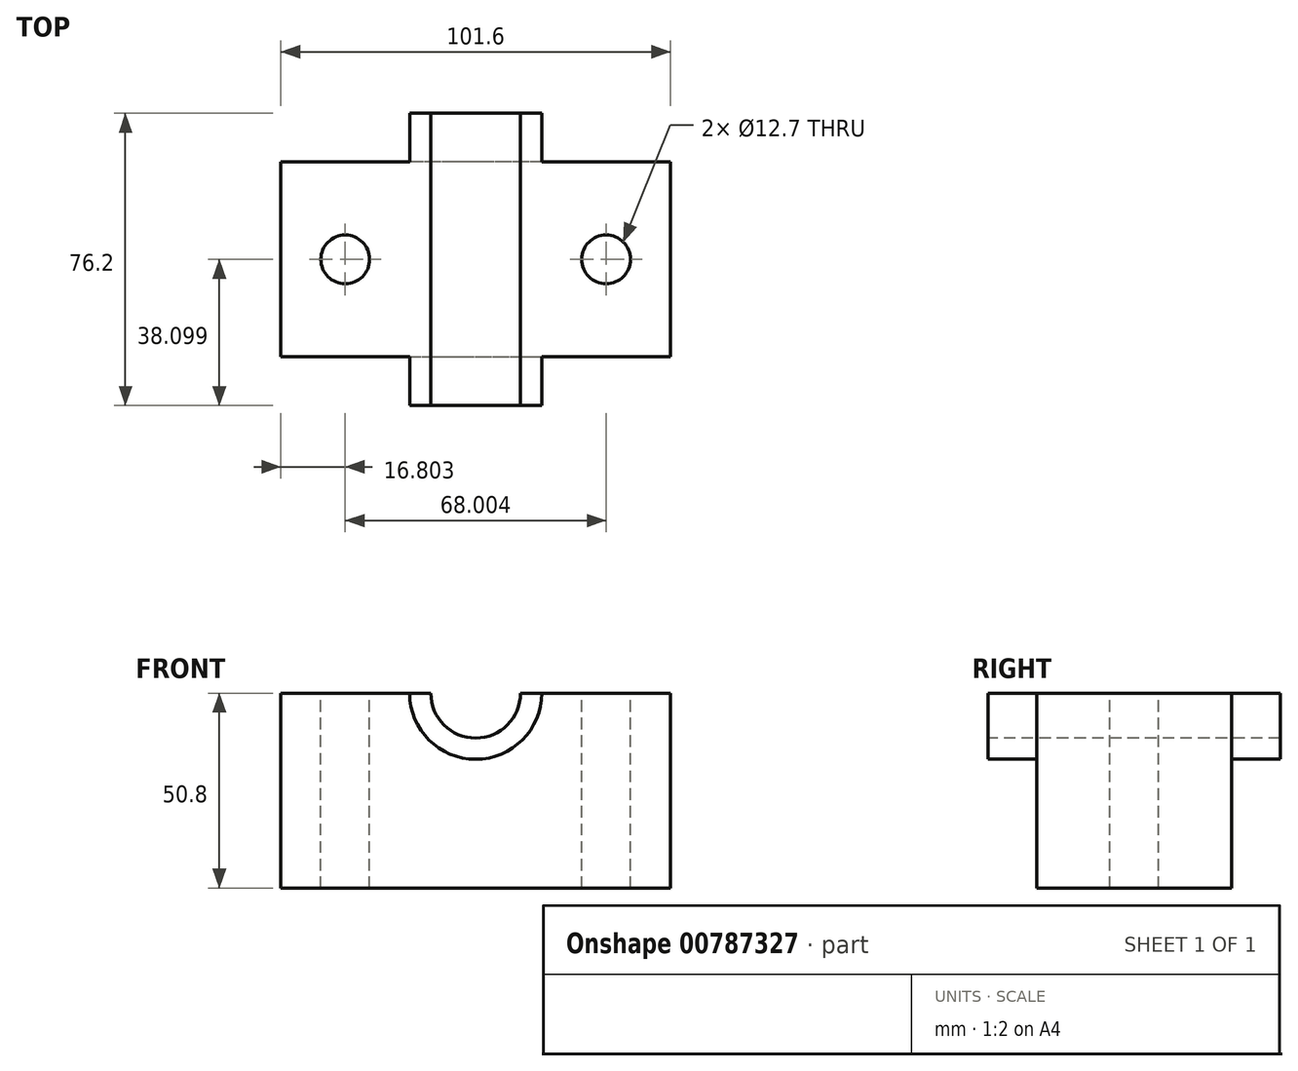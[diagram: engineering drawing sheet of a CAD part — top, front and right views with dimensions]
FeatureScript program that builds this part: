
annotation { "Feature Type Name" : "Feature", "Feature Type Description" : "" }
export const myFeature = defineFeature(function(context is Context, id is Id, definition is map)
    precondition{}
    {
        {
            var Q0;
            Q0=qCreatedBy(makeId("Top.planeOp"),FACE);
            var sketch = newSketch(context, id + "F0", { "sketchPlane" : qUnion([Q0])});
            skLineSegment(sketch, "E0", {"start": v(-63.02, 23.88) * mm, "end": v(-63.02, -26.92) * mm});
            skLineSegment(sketch, "E1", {"start": v(-63.02, -26.92) * mm, "end": v(38.58, -26.92) * mm});
            skLineSegment(sketch, "E2", {"start": v(38.58, -26.92) * mm, "end": v(38.58, 23.88) * mm});
            skLineSegment(sketch, "E3", {"start": v(38.58, 23.88) * mm, "end": v(-63.02, 23.88) * mm});
            skSolve(sketch);
        }
        {
            var Q0;
            Q0=makeQuery(id+"F0.imprint","IMPRINT",FACE,{"disambiguationData":[TD([[makeQuery(id+"F0.imprint","IMPRINT",EDGE,{"derivedFrom":sQuery(id+"F0.wireOp",EDGE,"E0")}),1.0]])]});
            extrude(context, id + "F1", {"entities" : qUnion([Q0]), "depth" : 50.8 * mm, "offsetDistance" : 25.4 * mm});
        }
        {
            var Q0;
            Q0=makeQuery(id+"F1.opExtrude","SWEPT_FACE",FACE,{"disambiguationData":[OSD([sQuery(id+"F0.wireOp",EDGE,"E1")])]});
            var sketch = newSketch(context, id + "F2", { "sketchPlane" : qUnion([Q0])});
            skArc(sketch, "E4", {"start": v(-29.43, 50.8) * mm, "mid": v(-12.22, 33.58) * mm, "end": v(5, 50.8) * mm});
            skArc(sketch, "E5", {"start": v(-23.9, 50.8) * mm, "mid": v(-12.22, 39.1) * mm, "end": v(-0.52, 50.8) * mm});
            skPoint(sketch, "E6.end.orphan", {"position": v(-12.22, 0) * mm});
            skSolve(sketch);
        }
        {
            var Q0;
            {var subQ0=sQuery(id+"F2.wireOp",EDGE,"E5");Q0=makeQuery(id+"F2.imprint","IMPRINT",FACE,{"disambiguationData":[TD([[makeQuery(id+"F2.imprint","IMPRINT",EDGE,{"derivedFrom":subQ0}),1.0]])]});}
            extrude(context, id + "F3", {"entities" : qUnion([Q0]), "operationType" : NewBodyOperationType.REMOVE, "oppositeDirection" : true, "depth" : 59.69 * mm, "offsetDistance" : 25.4 * mm});
        }
        {
            var Q0;
            {var subQ0=sQuery(id+"F2.wireOp",EDGE,"E4");Q0=makeQuery(id+"F2.imprint","IMPRINT",FACE,{"disambiguationData":[TD([[makeQuery(id+"F2.imprint","IMPRINT",EDGE,{"derivedFrom":subQ0}),1.0]])]});}
            extrude(context, id + "F4", {"entities" : qUnion([Q0]), "operationType" : NewBodyOperationType.ADD, "depth" : 12.7 * mm, "offsetDistance" : 25.4 * mm});
        }
        {
            var Q0;
            Q0=makeQuery(id+"F1.opExtrude","SWEPT_FACE",FACE,{"disambiguationData":[OSD([sQuery(id+"F0.wireOp",EDGE,"E3")])]});
            var sketch = newSketch(context, id + "F5", { "sketchPlane" : qUnion([Q0])});
            skArc(sketch, "E7", {"start": v(-4.99, 50.8) * mm, "mid": v(12.22, 33.6) * mm, "end": v(29.42, 50.8) * mm});
            skSolve(sketch);
        }
        {
            var Q0;
            {var subQ0=sQuery(id+"F5.wireOp",EDGE,"E7");Q0=makeQuery(id+"F5.imprint","IMPRINT",FACE,{"disambiguationData":[TD([[makeQuery(id+"F5.imprint","IMPRINT",EDGE,{"derivedFrom":subQ0}),1.0]])]});}
            extrude(context, id + "F6", {"entities" : qUnion([Q0]), "operationType" : NewBodyOperationType.ADD, "depth" : 12.7 * mm, "offsetDistance" : 25.4 * mm});
        }
        {
            var Q0;
            {var subQ0=sQuery(id+"F0.wireOp",EDGE,"E0");var subQ1=makeQuery(id+"F1.opExtrude","SWEPT_FACE",FACE,{"disambiguationData":[OSD([subQ0])]});var subQ2=sQuery(id+"F0.wireOp",EDGE,"E3");var subQ4=sQuery(id+"F0.wireOp",EDGE,"E1");var subQ5=makeQuery(id+"F1.opExtrude","CAP_FACE",FACE,{"disambiguationData":[OSD([subQ0,subQ4,sQuery(id+"F0.wireOp",EDGE,"E2"),subQ2])],"isStart":false});var subQ8=makeQuery(id+"F3.boolean.opBoolean","SPLIT",EDGE,{"disambiguationData":[TD([subQ1])],"derivedFrom":makeQuery(id+"F1.opExtrude","CAP_EDGE",EDGE,{"disambiguationData":[OSD([subQ2])],"isStart":false})});var subQ9=makeQuery(id+"F1.opExtrude","CAP_EDGE",EDGE,{"disambiguationData":[OSD([subQ4])],"isStart":false});Q0=makeQuery(id+"F6.boolean.opBoolean","MERGE",FACE,{"derivedFrom":[makeQuery(id+"F4.boolean.opBoolean","MERGE",FACE,{"derivedFrom":[makeQuery(id+"F3.boolean.opBoolean","SPLIT",FACE,{"disambiguationData":[TD([subQ1])],"derivedFrom":subQ5}),makeQuery(id+"F4.opExtrude","SWEPT_FACE",FACE,{"disambiguationData":[OSD([subQ4]),TDD([makeQuery(id+"F2.imprint","IMPRINT",EDGE,{"disambiguationData":[TD([[makeQuery(id+"F2.imprint","INTERSECT",VERTEX,{"disambiguationData":[OD(0.0)],"derivedFrom":[subQ9,sQuery(id+"F2.wireOp",EDGE,"E4")]}),-1.0]])],"derivedFrom":subQ9})])]})]}),makeQuery(id+"F6.opExtrude","SWEPT_FACE",FACE,{"disambiguationData":[OSD([subQ2]),TDD([makeQuery(id+"F5.imprint","IMPRINT",EDGE,{"disambiguationData":[TD([[makeQuery(id+"F5.imprint","INTERSECT",VERTEX,{"derivedFrom":[subQ8,sQuery(id+"F5.wireOp",EDGE,"E7")]}),1.0]])],"derivedFrom":subQ8})])]})]});}
            var sketch = newSketch(context, id + "F7", { "sketchPlane" : qUnion([Q0])});
            skCircle(sketch, "E8", {"center": v(-46.22, -1.52) * mm, "radius": 6.35 * mm});
            skSolve(sketch);
        }
        {
            var Q0;
            Q0=makeQuery(id+"F7.imprint","IMPRINT",FACE,{"disambiguationData":[TD([[makeQuery(id+"F7.imprint","IMPRINT",EDGE,{"derivedFrom":sQuery(id+"F7.wireOp",EDGE,"E8")}),1.0]])]});
            extrude(context, id + "F8", {"entities" : qUnion([Q0]), "operationType" : NewBodyOperationType.REMOVE, "oppositeDirection" : true, "depth" : 67.82 * mm, "offsetDistance" : 25.4 * mm});
        }
        {
            var Q0;
            {var subQ0=sQuery(id+"F0.wireOp",EDGE,"E3");var subQ1=sQuery(id+"F0.wireOp",EDGE,"E2");var subQ2=sQuery(id+"F0.wireOp",EDGE,"E1");var subQ3=makeQuery(id+"F1.opExtrude","CAP_FACE",FACE,{"disambiguationData":[OSD([sQuery(id+"F0.wireOp",EDGE,"E0"),subQ2,subQ1,subQ0])],"isStart":false});var subQ4=makeQuery(id+"F1.opExtrude","SWEPT_FACE",FACE,{"disambiguationData":[OSD([subQ1])]});var subQ8=makeQuery(id+"F3.boolean.opBoolean","SPLIT",EDGE,{"disambiguationData":[TD([subQ4])],"derivedFrom":makeQuery(id+"F1.opExtrude","CAP_EDGE",EDGE,{"disambiguationData":[OSD([subQ0])],"isStart":false})});var subQ9=makeQuery(id+"F1.opExtrude","CAP_EDGE",EDGE,{"disambiguationData":[OSD([subQ2])],"isStart":false});Q0=makeQuery(id+"F6.boolean.opBoolean","MERGE",FACE,{"derivedFrom":[makeQuery(id+"F4.boolean.opBoolean","MERGE",FACE,{"derivedFrom":[makeQuery(id+"F3.boolean.opBoolean","SPLIT",FACE,{"disambiguationData":[TD([subQ4])],"derivedFrom":subQ3}),makeQuery(id+"F4.opExtrude","SWEPT_FACE",FACE,{"disambiguationData":[OSD([subQ2]),TDD([makeQuery(id+"F2.imprint","IMPRINT",EDGE,{"disambiguationData":[TD([[makeQuery(id+"F2.imprint","INTERSECT",VERTEX,{"disambiguationData":[OD(1.0)],"derivedFrom":[subQ9,sQuery(id+"F2.wireOp",EDGE,"E4")]}),1.0]])],"derivedFrom":subQ9})])]})]}),makeQuery(id+"F6.opExtrude","SWEPT_FACE",FACE,{"disambiguationData":[OSD([subQ0]),TDD([makeQuery(id+"F5.imprint","IMPRINT",EDGE,{"disambiguationData":[TD([[makeQuery(id+"F5.imprint","INTERSECT",VERTEX,{"derivedFrom":[subQ8,sQuery(id+"F5.wireOp",EDGE,"E7")]}),-1.0]])],"derivedFrom":subQ8})])]})]});}
            var sketch = newSketch(context, id + "F9", { "sketchPlane" : qUnion([Q0])});
            skCircle(sketch, "E9", {"center": v(21.79, -1.52) * mm, "radius": 6.35 * mm});
            skSolve(sketch);
        }
        {
            var Q0;
            Q0=makeQuery(id+"F9.imprint","IMPRINT",FACE,{"disambiguationData":[TD([[makeQuery(id+"F9.imprint","IMPRINT",EDGE,{"derivedFrom":sQuery(id+"F9.wireOp",EDGE,"E9")}),1.0]])]});
            extrude(context, id + "F10", {"entities" : qUnion([Q0]), "operationType" : NewBodyOperationType.REMOVE, "oppositeDirection" : true, "depth" : 76.2 * mm, "offsetDistance" : 25.4 * mm});
        }
    });
